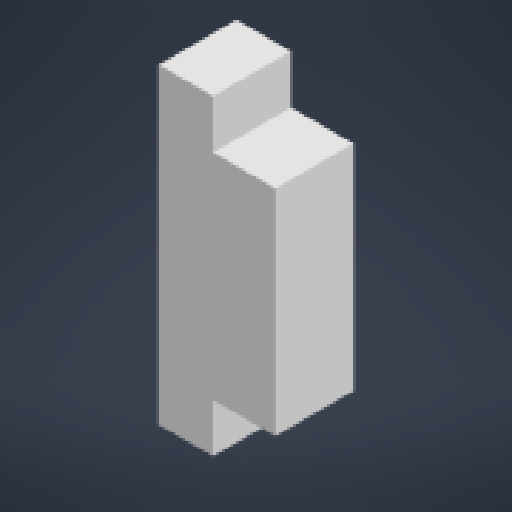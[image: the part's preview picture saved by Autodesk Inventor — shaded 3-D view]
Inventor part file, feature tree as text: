
AUTODESK INVENTOR PART (.ipt)
format: ipt  version: 2023 (Build 270158000, 158)  size: 120,320 bytes
history: native  units: in
note: dims shown in document units (in); Inventor stores cm internally (conversion verified against a paired STEP export)
features: extrude x1, sketch x1
ambient origin geometry x8: Origin, YZ Plane, XZ Plane, XY Plane, X Axis, Y Axis, Z Axis, Center Point
bodies: Solid1 (feature_tree)
feature tree (2):
  extrude  "Extrusion1"  Depth=0.063in
  sketch  "Sketch1"  dims[d0=0.011in d1=0.063in d2=0.0126in d3=0.0217in d4=0.0217in d5=0.0157in d6=0.0in]
